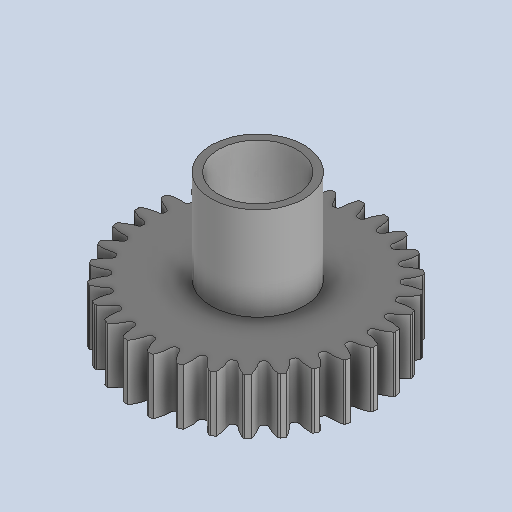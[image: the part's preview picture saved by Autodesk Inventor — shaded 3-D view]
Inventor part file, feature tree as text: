
AUTODESK INVENTOR PART (.ipt)
format: ipt  version: 2024 (Build 280153000, 153)  size: 723,968 bytes
history: native  units: mm
features: extrude x5, sketch x4, pattern_circular x2, fillet x1, revolve x1, plane x1, other x1, projected_geometry x1
ambient origin geometry x8: Origin, YZ Plane, XZ Plane, XY Plane, X Axis, Y Axis, Z Axis, Center Point
bodies: Body1 (feature_tree), Body2 (feature_tree)
feature tree (16):
  sketch  "Sketch4"  dims[d10=15.0mm d11=0.0mm d12=0.0mm d13=0.0mm]
  extrude  "Extrusion4"  TaperAngle=0.0deg  [1 undecoded]
  extrude  "Extrusion5"  Depth=0.5mm
  pattern_circular  "Circular Pattern1"  Count=30 Angle=360.0deg
  fillet  "Fillet1"  Radius=6.35mm
  pattern_circular  "Circular Pattern2"  Count=2  [1 undecoded]
  revolve  "Revolution1"  [1 undecoded]
  plane  "Work Plane1"
  extrude  "Extrusion11"  Depth=25.0mm
  extrude  "Extrusion12"  Depth=25.0mm TaperAngle=0.0deg
  other  "Srf1"
  sketch  "Sketch8"  dims[d14=300.0mm d15=360.0deg d26=0.5mm d27=300.0mm d28=360.0deg d30=0.0mm d31=0.0mm d32=6.35mm d33=20.0mm]
  sketch  "Sketch11"  dims[d34=360.0deg d35=-7.5mm]
  sketch  "Sketch12"  dims[d42=25.0mm d43=2.0mm d44=25.0mm d45=0.0mm d46=0.0mm d47=0.0mm d37=0.5mm d38=0.872665mm d39=0.5mm d40=0.872665mm d48=0.5mm d49=0.872665mm d50=0.5mm d51=0.872665mm]
  projected_geometry  "Projected Loop2"
  extrude  "ExtrusionSrf1"  TaperAngle=0.0deg  [1 undecoded]
note: 4 required parameter values undecoded (feature->parameter linkage not recoverable at this tier; creation-order binding heuristic only, values carry confidence <= 0.55)